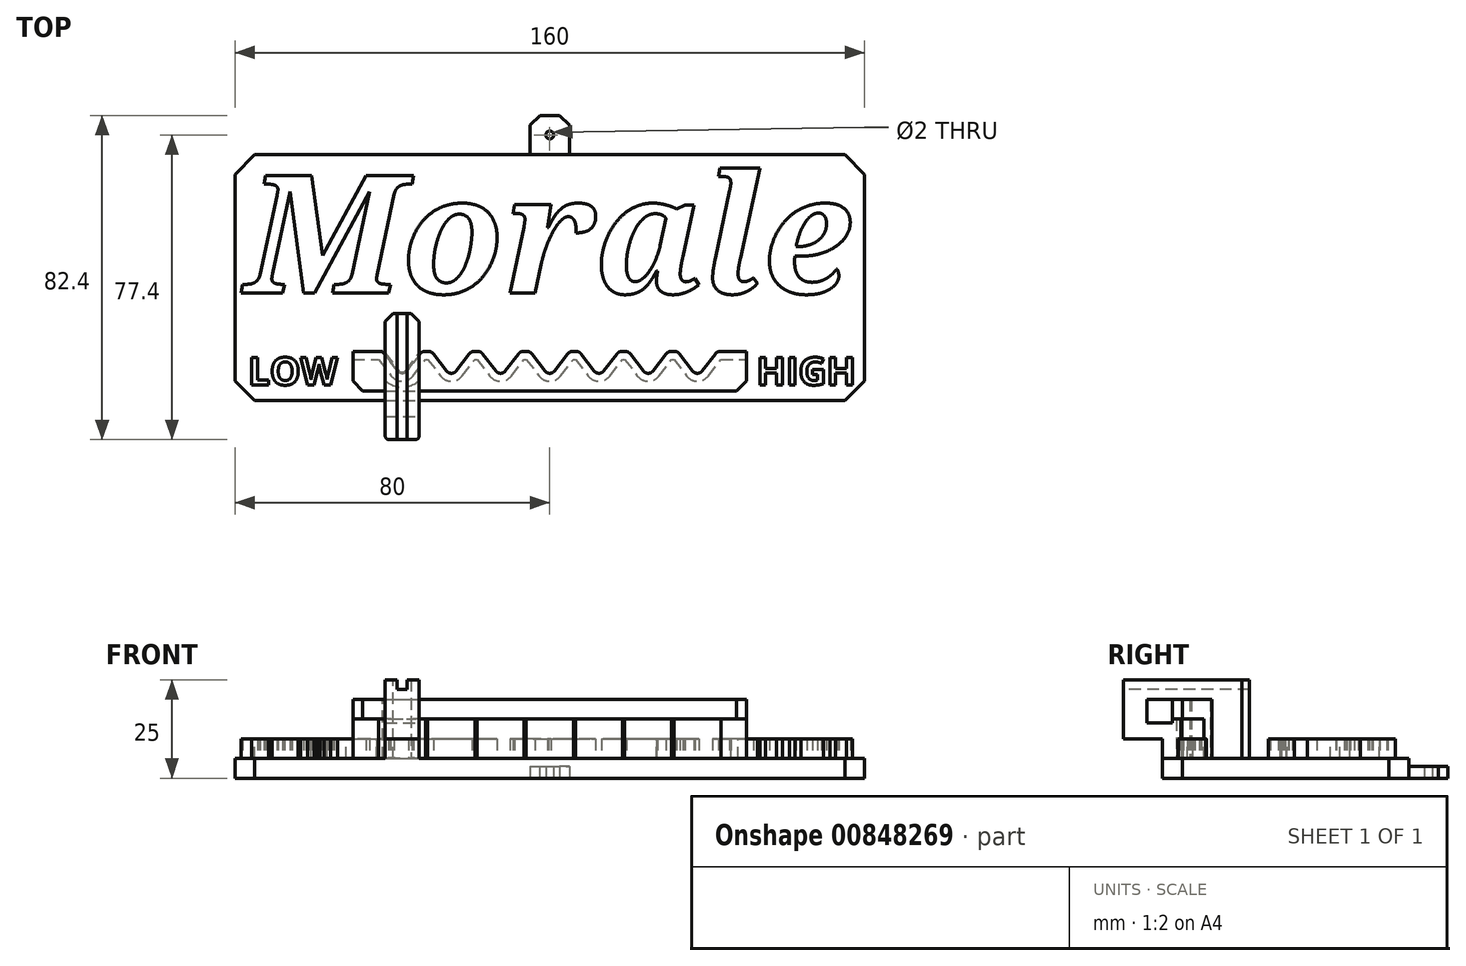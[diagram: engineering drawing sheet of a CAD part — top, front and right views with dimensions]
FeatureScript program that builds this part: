
annotation { "Feature Type Name" : "Feature", "Feature Type Description" : "" }
export const myFeature = defineFeature(function(context is Context, id is Id, definition is map)
    precondition{}
    {
        {
            var Q0;
            Q0=qCreatedBy(makeId("Top.planeOp"),FACE);
            var sketch = newSketch(context, id + "F0", { "sketchPlane" : qUnion([Q0])});
            skLineSegment(sketch, "E0.bottom", {"start": v(0, 0) * mm, "end": v(160, 0) * mm});
            skLineSegment(sketch, "E0.top", {"start": v(0, 37.5) * mm, "end": v(160, 37.5) * mm});
            skLineSegment(sketch, "E0.left", {"start": v(0, 0) * mm, "end": v(0, 37.5) * mm});
            skLineSegment(sketch, "E0.right", {"start": v(160, 0) * mm, "end": v(160, 37.5) * mm});
            skSolve(sketch);
        }
        {
            var Q0;
            Q0 = qSketchRegion(id + "F0", true);
            extrude(context, id + "F1", {"entities" : qUnion([Q0]), "depth" : 5 * mm, "offsetDistance" : 25 * mm});
        }
        {
            var Q0;
            Q0=makeQuery(id+"F1.opExtrude","CAP_FACE",FACE,{"disambiguationData":[OSD([sQuery(id+"F0.wireOp",EDGE,"E0.bottom"),sQuery(id+"F0.wireOp",EDGE,"E0.top"),sQuery(id+"F0.wireOp",EDGE,"E0.left"),sQuery(id+"F0.wireOp",EDGE,"E0.right")])],"isStart":false});
            var sketch = newSketch(context, id + "F2", { "sketchPlane" : qUnion([Q0])});
            skText(sketch, "E1", { "text": "Morale", "fontName": "NotoSerif-BoldItalic.ttf"});
            const initialGuessF2  = {"E1": [0.0025, 0.00232, 1, 0, 0.03018]};
            skSetInitialGuess(sketch, initialGuessF2);
            skSolve(sketch);
        }
        {
            var Q0;
            Q0 = qSketchRegion(id + "F2", true);
            extrude(context, id + "F3", {"entities" : qUnion([Q0]), "operationType" : NewBodyOperationType.ADD, "depth" : 5 * mm, "offsetDistance" : 25 * mm});
        }
        {
            var Q0;
            Q0=makeQuery(id+"F1.opExtrude","SWEPT_FACE",FACE,{"disambiguationData":[OSD([sQuery(id+"F0.wireOp",EDGE,"E0.bottom")])]});
            extrude(context, id + "F4", {"entities" : qUnion([Q0]), "operationType" : NewBodyOperationType.ADD, "depth" : 25 * mm, "offsetDistance" : 25 * mm});
        }
        {
            var Q0;
            {var subQ0=sQuery(id+"F0.wireOp",EDGE,"E0.bottom");var subQ1=sQuery(id+"F0.wireOp",EDGE,"E0.left");var subQ2=sQuery(id+"F0.wireOp",EDGE,"E0.right");var subQ3=sQuery(id+"F0.wireOp",EDGE,"E0.top");Q0=makeQuery(id+"F4.boolean.opBoolean","MERGE",FACE,{"derivedFrom":[makeQuery(id+"F3.boolean.opBoolean","SPLIT",FACE,{"disambiguationData":[TD([makeQuery(id+"F1.opExtrude","SWEPT_FACE",FACE,{"disambiguationData":[OSD([subQ0])]})])],"derivedFrom":makeQuery(id+"F1.opExtrude","CAP_FACE",FACE,{"disambiguationData":[OSD([subQ0,subQ3,subQ1,subQ2])],"isStart":false})}),makeQuery(id+"F4.opExtrude","SWEPT_FACE",FACE,{"disambiguationData":[OSD([subQ0]),TDD([makeQuery(id+"F1.opExtrude","CAP_EDGE",EDGE,{"disambiguationData":[OSD([subQ0])],"isStart":false})])]})]});}
            var sketch = newSketch(context, id + "F5", { "sketchPlane" : qUnion([Q0])});
            skLineSegment(sketch, "E2.bottom", {"start": v(30, -22.5) * mm, "end": v(130, -22.5) * mm});
            skLineSegment(sketch, "E2.top", {"start": v(30, -12.5) * mm, "end": v(130, -12.5) * mm});
            skLineSegment(sketch, "E2.left", {"start": v(30, -22.5) * mm, "end": v(30, -12.5) * mm});
            skLineSegment(sketch, "E2.right", {"start": v(130, -22.5) * mm, "end": v(130, -12.5) * mm});
            skPoint(sketch, "E2.middle", {"position": v(80, -17.5) * mm});
            skPoint(sketch, "E2.middle.positionSnap0", {"position": v(80, -25) * mm});
            skPoint(sketch, "E2.centerSnap0", {"position": v(80, -25) * mm});
            skSolve(sketch);
        }
        {
            var Q0;
            Q0 = qSketchRegion(id + "F5", true);
            extrude(context, id + "F6", {"entities" : qUnion([Q0]), "operationType" : NewBodyOperationType.ADD, "depth" : 15 * mm, "offsetDistance" : 25 * mm});
        }
        {
            var Q0;
            Q0=makeQuery(id+"F6.opExtrude","CAP_FACE",FACE,{"disambiguationData":[OSD([sQuery(id+"F5.wireOp",EDGE,"E2.bottom"),sQuery(id+"F5.wireOp",EDGE,"E2.top"),sQuery(id+"F5.wireOp",EDGE,"E2.left"),sQuery(id+"F5.wireOp",EDGE,"E2.right")])],"isStart":false});
            var sketch = newSketch(context, id + "F7", { "sketchPlane" : qUnion([Q0])});
            skLineSegment(sketch, "E3", {"start": v(37.5, -12.5) * mm, "end": v(42.5, -19.02) * mm});
            skLineSegment(sketch, "E4", {"start": v(42.5, -19.02) * mm, "end": v(47.5, -12.5) * mm});
            skLineSegment(sketch, "E5", {"start": v(37.5, -12.5) * mm, "end": v(47.5, -12.5) * mm});
            skLineSegment(sketch, "E6.1.0.0", {"start": v(50, -12.5) * mm, "end": v(60, -12.5) * mm});
            skLineSegment(sketch, "E6.1.0.1", {"start": v(55, -19.02) * mm, "end": v(60, -12.5) * mm});
            skLineSegment(sketch, "E6.1.0.2", {"start": v(50, -12.5) * mm, "end": v(55, -19.02) * mm});
            skLineSegment(sketch, "E6.2.0.0", {"start": v(62.5, -12.5) * mm, "end": v(72.5, -12.5) * mm});
            skLineSegment(sketch, "E6.2.0.1", {"start": v(67.5, -19.02) * mm, "end": v(72.5, -12.5) * mm});
            skLineSegment(sketch, "E6.2.0.2", {"start": v(62.5, -12.5) * mm, "end": v(67.5, -19.02) * mm});
            skLineSegment(sketch, "E6.3.0.0", {"start": v(75, -12.5) * mm, "end": v(85, -12.5) * mm});
            skLineSegment(sketch, "E6.3.0.1", {"start": v(80, -19.02) * mm, "end": v(85, -12.5) * mm});
            skLineSegment(sketch, "E6.3.0.2", {"start": v(75, -12.5) * mm, "end": v(80, -19.02) * mm});
            skLineSegment(sketch, "E6.4.0.0", {"start": v(87.5, -12.5) * mm, "end": v(97.5, -12.5) * mm});
            skLineSegment(sketch, "E6.4.0.1", {"start": v(92.5, -19.02) * mm, "end": v(97.5, -12.5) * mm});
            skLineSegment(sketch, "E6.4.0.2", {"start": v(87.5, -12.5) * mm, "end": v(92.5, -19.02) * mm});
            skLineSegment(sketch, "E6.5.0.0", {"start": v(100, -12.5) * mm, "end": v(110, -12.5) * mm});
            skLineSegment(sketch, "E6.5.0.1", {"start": v(105, -19.02) * mm, "end": v(110, -12.5) * mm});
            skLineSegment(sketch, "E6.5.0.2", {"start": v(100, -12.5) * mm, "end": v(105, -19.02) * mm});
            skLineSegment(sketch, "E6.6.0.0", {"start": v(112.5, -12.5) * mm, "end": v(122.5, -12.5) * mm});
            skLineSegment(sketch, "E6.6.0.1", {"start": v(117.5, -19.02) * mm, "end": v(122.5, -12.5) * mm});
            skLineSegment(sketch, "E6.6.0.2", {"start": v(112.5, -12.5) * mm, "end": v(117.5, -19.02) * mm});
            skLineSegment(sketch, "E6.direction1", {"start": v(42.5, -19.02) * mm, "end": v(55, -19.02) * mm, "construction": true});
            skSolve(sketch);
        }
        {
            var Q0;
            Q0 = qSketchRegion(id + "F7", true);
            var Q1;
            {var subQ0=sQuery(id+"F0.wireOp",EDGE,"E0.bottom");var subQ1=sQuery(id+"F0.wireOp",EDGE,"E0.left");var subQ2=sQuery(id+"F0.wireOp",EDGE,"E0.right");var subQ3=sQuery(id+"F0.wireOp",EDGE,"E0.top");Q1=makeQuery(id+"F4.boolean.opBoolean","MERGE",FACE,{"derivedFrom":[makeQuery(id+"F3.boolean.opBoolean","SPLIT",FACE,{"disambiguationData":[TD([makeQuery(id+"F1.opExtrude","SWEPT_FACE",FACE,{"disambiguationData":[OSD([subQ0])]})])],"derivedFrom":makeQuery(id+"F1.opExtrude","CAP_FACE",FACE,{"disambiguationData":[OSD([subQ0,subQ3,subQ1,subQ2])],"isStart":false})}),makeQuery(id+"F4.opExtrude","SWEPT_FACE",FACE,{"disambiguationData":[OSD([subQ0]),TDD([makeQuery(id+"F1.opExtrude","CAP_EDGE",EDGE,{"disambiguationData":[OSD([subQ0])],"isStart":false})])]})]});}
            extrude(context, id + "F8", {"entities" : qUnion([Q0]), "operationType" : NewBodyOperationType.REMOVE, "endBound" : BoundingType.UP_TO_SURFACE, "oppositeDirection" : true, "depth" : 25 * mm, "endBoundEntityFace" : qUnion([Q1]), "offsetDistance" : 25 * mm});
        }
        {
            var Q0;
            {var subQ0=sQuery(id+"F0.wireOp",EDGE,"E0.bottom");var subQ1=sQuery(id+"F0.wireOp",EDGE,"E0.left");var subQ2=sQuery(id+"F0.wireOp",EDGE,"E0.right");var subQ3=sQuery(id+"F0.wireOp",EDGE,"E0.top");Q0=makeQuery(id+"F8.boolean.opBoolean","MERGE",FACE,{"derivedFrom":[makeQuery(id+"F4.boolean.opBoolean","MERGE",FACE,{"derivedFrom":[makeQuery(id+"F3.boolean.opBoolean","SPLIT",FACE,{"disambiguationData":[TD([makeQuery(id+"F1.opExtrude","SWEPT_FACE",FACE,{"disambiguationData":[OSD([subQ0])]})])],"derivedFrom":makeQuery(id+"F1.opExtrude","CAP_FACE",FACE,{"disambiguationData":[OSD([subQ0,subQ3,subQ1,subQ2])],"isStart":false})}),makeQuery(id+"F4.opExtrude","SWEPT_FACE",FACE,{"disambiguationData":[OSD([subQ0]),TDD([makeQuery(id+"F1.opExtrude","CAP_EDGE",EDGE,{"disambiguationData":[OSD([subQ0])],"isStart":false})])]})]})],"fromTools":[makeQuery(id+"F8.opExtrude","CAP_FACE",FACE,{"disambiguationData":[OSD([sQuery(id+"F7.wireOp",EDGE,"E3"),sQuery(id+"F7.wireOp",EDGE,"E4"),sQuery(id+"F7.wireOp",EDGE,"E5")])],"isStart":false}),makeQuery(id+"F8.opExtrude","CAP_FACE",FACE,{"disambiguationData":[OSD([sQuery(id+"F7.wireOp",EDGE,"E6.1.0.0"),sQuery(id+"F7.wireOp",EDGE,"E6.1.0.1"),sQuery(id+"F7.wireOp",EDGE,"E6.1.0.2")])],"isStart":false}),makeQuery(id+"F8.opExtrude","CAP_FACE",FACE,{"disambiguationData":[OSD([sQuery(id+"F7.wireOp",EDGE,"E6.2.0.0"),sQuery(id+"F7.wireOp",EDGE,"E6.2.0.1"),sQuery(id+"F7.wireOp",EDGE,"E6.2.0.2")])],"isStart":false}),makeQuery(id+"F8.opExtrude","CAP_FACE",FACE,{"disambiguationData":[OSD([sQuery(id+"F7.wireOp",EDGE,"E6.3.0.0"),sQuery(id+"F7.wireOp",EDGE,"E6.3.0.1"),sQuery(id+"F7.wireOp",EDGE,"E6.3.0.2")])],"isStart":false}),makeQuery(id+"F8.opExtrude","CAP_FACE",FACE,{"disambiguationData":[OSD([sQuery(id+"F7.wireOp",EDGE,"E6.4.0.0"),sQuery(id+"F7.wireOp",EDGE,"E6.4.0.1"),sQuery(id+"F7.wireOp",EDGE,"E6.4.0.2")])],"isStart":false}),makeQuery(id+"F8.opExtrude","CAP_FACE",FACE,{"disambiguationData":[OSD([sQuery(id+"F7.wireOp",EDGE,"E6.5.0.0"),sQuery(id+"F7.wireOp",EDGE,"E6.5.0.1"),sQuery(id+"F7.wireOp",EDGE,"E6.5.0.2")])],"isStart":false}),makeQuery(id+"F8.opExtrude","CAP_FACE",FACE,{"disambiguationData":[OSD([sQuery(id+"F7.wireOp",EDGE,"E6.6.0.0"),sQuery(id+"F7.wireOp",EDGE,"E6.6.0.1"),sQuery(id+"F7.wireOp",EDGE,"E6.6.0.2")])],"isStart":false})]});}
            var sketch = newSketch(context, id + "F9", { "sketchPlane" : qUnion([Q0])});
            skText(sketch, "E7", { "text": "LOW", "fontName": "OpenSans-Bold.ttf"});
            skText(sketch, "E8", { "text": "HIGH", "fontName": "OpenSans-Bold.ttf"});
            const initialGuessF9  = {"E7": [0.00338, -0.021, 1, 0, 0.00703], "E8": [0.1325, -0.021, 1, 0, 0.00703]};
            skSetInitialGuess(sketch, initialGuessF9);
            skSolve(sketch);
        }
        {
            var Q0;
            Q0 = qSketchRegion(id + "F9", true);
            var Q1;
            Q1=makeQuery(id+"F3.opExtrude","CAP_FACE",FACE,{"disambiguationData":[OSD([sQuery(id+"F2.wireOp",EDGE,"E1.sketch_text.stroke-203"),sQuery(id+"F2.wireOp",EDGE,"E1.sketch_text.stroke-204"),sQuery(id+"F2.wireOp",EDGE,"E1.sketch_text.stroke-205"),sQuery(id+"F2.wireOp",EDGE,"E1.sketch_text.stroke-206"),sQuery(id+"F2.wireOp",EDGE,"E1.sketch_text.stroke-207"),sQuery(id+"F2.wireOp",EDGE,"E1.sketch_text.stroke-208"),sQuery(id+"F2.wireOp",EDGE,"E1.sketch_text.stroke-209"),sQuery(id+"F2.wireOp",EDGE,"E1.sketch_text.stroke-210"),sQuery(id+"F2.wireOp",EDGE,"E1.sketch_text.stroke-211"),sQuery(id+"F2.wireOp",EDGE,"E1.sketch_text.stroke-212"),sQuery(id+"F2.wireOp",EDGE,"E1.sketch_text.stroke-213"),sQuery(id+"F2.wireOp",EDGE,"E1.sketch_text.stroke-214"),sQuery(id+"F2.wireOp",EDGE,"E1.sketch_text.stroke-215"),sQuery(id+"F2.wireOp",EDGE,"E1.sketch_text.stroke-216"),sQuery(id+"F2.wireOp",EDGE,"E1.sketch_text.stroke-217"),sQuery(id+"F2.wireOp",EDGE,"E1.sketch_text.stroke-218"),sQuery(id+"F2.wireOp",EDGE,"E1.sketch_text.stroke-219"),sQuery(id+"F2.wireOp",EDGE,"E1.sketch_text.stroke-220"),sQuery(id+"F2.wireOp",EDGE,"E1.sketch_text.stroke-221"),sQuery(id+"F2.wireOp",EDGE,"E1.sketch_text.stroke-222"),sQuery(id+"F2.wireOp",EDGE,"E1.sketch_text.stroke-223"),sQuery(id+"F2.wireOp",EDGE,"E1.sketch_text.stroke-224"),sQuery(id+"F2.wireOp",EDGE,"E1.sketch_text.stroke-225"),sQuery(id+"F2.wireOp",EDGE,"E1.sketch_text.stroke-226"),sQuery(id+"F2.wireOp",EDGE,"E1.sketch_text.stroke-227"),sQuery(id+"F2.wireOp",EDGE,"E1.sketch_text.stroke-228"),sQuery(id+"F2.wireOp",EDGE,"E1.sketch_text.stroke-229"),sQuery(id+"F2.wireOp",EDGE,"E1.sketch_text.stroke-230"),sQuery(id+"F2.wireOp",EDGE,"E1.sketch_text.stroke-231"),sQuery(id+"F2.wireOp",EDGE,"E1.sketch_text.stroke-232"),sQuery(id+"F2.wireOp",EDGE,"E1.sketch_text.stroke-233"),sQuery(id+"F2.wireOp",EDGE,"E1.sketch_text.stroke-234"),sQuery(id+"F2.wireOp",EDGE,"E1.sketch_text.stroke-235"),sQuery(id+"F2.wireOp",EDGE,"E1.sketch_text.stroke-236"),sQuery(id+"F2.wireOp",EDGE,"E1.sketch_text.stroke-237"),sQuery(id+"F2.wireOp",EDGE,"E1.sketch_text.stroke-238"),sQuery(id+"F2.wireOp",EDGE,"E1.sketch_text.stroke-239"),sQuery(id+"F2.wireOp",EDGE,"E1.sketch_text.stroke-240"),sQuery(id+"F2.wireOp",EDGE,"E1.sketch_text.stroke-241"),sQuery(id+"F2.wireOp",EDGE,"E1.sketch_text.stroke-242"),sQuery(id+"F2.wireOp",EDGE,"E1.sketch_text.stroke-243"),sQuery(id+"F2.wireOp",EDGE,"E1.sketch_text.stroke-244"),sQuery(id+"F2.wireOp",EDGE,"E1.sketch_text.stroke-245")])],"isStart":false});
            extrude(context, id + "F10", {"entities" : qUnion([Q0]), "operationType" : NewBodyOperationType.ADD, "endBound" : BoundingType.UP_TO_SURFACE, "depth" : 25 * mm, "endBoundEntityFace" : qUnion([Q1]), "offsetDistance" : 25 * mm});
        }
        {
            var Q0;
            Q0=makeQuery(id+"F8.boolean.opBoolean","COPY",EDGE,{"derivedFrom":makeQuery(id+"F8.opExtrude","SWEPT_EDGE",EDGE,{"disambiguationData":[OSD([sQuery(id+"F7.wireOp",EDGE,"E6.5.0.1"),sQuery(id+"F7.wireOp",EDGE,"E6.5.0.2")])]})});
            var Q1;
            Q1=makeQuery(id+"F8.boolean.opBoolean","COPY",EDGE,{"derivedFrom":makeQuery(id+"F8.opExtrude","SWEPT_EDGE",EDGE,{"disambiguationData":[OSD([sQuery(id+"F7.wireOp",EDGE,"E6.6.0.1"),sQuery(id+"F7.wireOp",EDGE,"E6.6.0.2")])]})});
            var Q2;
            Q2=makeQuery(id+"F8.boolean.opBoolean","COPY",EDGE,{"derivedFrom":makeQuery(id+"F8.opExtrude","SWEPT_EDGE",EDGE,{"disambiguationData":[OSD([sQuery(id+"F7.wireOp",EDGE,"E6.4.0.1"),sQuery(id+"F7.wireOp",EDGE,"E6.4.0.2")])]})});
            var Q3;
            Q3=makeQuery(id+"F8.boolean.opBoolean","COPY",EDGE,{"derivedFrom":makeQuery(id+"F8.opExtrude","SWEPT_EDGE",EDGE,{"disambiguationData":[OSD([sQuery(id+"F7.wireOp",EDGE,"E6.3.0.1"),sQuery(id+"F7.wireOp",EDGE,"E6.3.0.2")])]})});
            var Q4;
            Q4=makeQuery(id+"F8.boolean.opBoolean","COPY",EDGE,{"derivedFrom":makeQuery(id+"F8.opExtrude","SWEPT_EDGE",EDGE,{"disambiguationData":[OSD([sQuery(id+"F7.wireOp",EDGE,"E6.2.0.1"),sQuery(id+"F7.wireOp",EDGE,"E6.2.0.2")])]})});
            var Q5;
            Q5=makeQuery(id+"F8.boolean.opBoolean","COPY",EDGE,{"derivedFrom":makeQuery(id+"F8.opExtrude","SWEPT_EDGE",EDGE,{"disambiguationData":[OSD([sQuery(id+"F7.wireOp",EDGE,"E6.1.0.1"),sQuery(id+"F7.wireOp",EDGE,"E6.1.0.2")])]})});
            var Q6;
            Q6=makeQuery(id+"F8.boolean.opBoolean","COPY",EDGE,{"derivedFrom":makeQuery(id+"F8.opExtrude","SWEPT_EDGE",EDGE,{"disambiguationData":[OSD([sQuery(id+"F7.wireOp",EDGE,"E3"),sQuery(id+"F7.wireOp",EDGE,"E4")])]})});
            var Q7;
            Q7=makeQuery(id+"F8.boolean.opBoolean","COPY",EDGE,{"derivedFrom":makeQuery(id+"F8.opExtrude","SWEPT_EDGE",EDGE,{"disambiguationData":[OSD([sQuery(id+"F5.wireOp",EDGE,"E2.top"),sQuery(id+"F7.wireOp",EDGE,"E6.6.0.0"),sQuery(id+"F7.wireOp",EDGE,"E6.6.0.1")])]})});
            var Q8;
            Q8=makeQuery(id+"F8.boolean.opBoolean","COPY",EDGE,{"derivedFrom":makeQuery(id+"F8.opExtrude","SWEPT_EDGE",EDGE,{"disambiguationData":[OSD([sQuery(id+"F5.wireOp",EDGE,"E2.top"),sQuery(id+"F7.wireOp",EDGE,"E6.6.0.0"),sQuery(id+"F7.wireOp",EDGE,"E6.6.0.2")])]})});
            var Q9;
            Q9=makeQuery(id+"F8.boolean.opBoolean","COPY",EDGE,{"derivedFrom":makeQuery(id+"F8.opExtrude","SWEPT_EDGE",EDGE,{"disambiguationData":[OSD([sQuery(id+"F5.wireOp",EDGE,"E2.top"),sQuery(id+"F7.wireOp",EDGE,"E6.5.0.0"),sQuery(id+"F7.wireOp",EDGE,"E6.5.0.1")])]})});
            var Q10;
            Q10=makeQuery(id+"F8.boolean.opBoolean","COPY",EDGE,{"derivedFrom":makeQuery(id+"F8.opExtrude","SWEPT_EDGE",EDGE,{"disambiguationData":[OSD([sQuery(id+"F5.wireOp",EDGE,"E2.top"),sQuery(id+"F7.wireOp",EDGE,"E6.5.0.0"),sQuery(id+"F7.wireOp",EDGE,"E6.5.0.2")])]})});
            var Q11;
            Q11=makeQuery(id+"F8.boolean.opBoolean","COPY",EDGE,{"derivedFrom":makeQuery(id+"F8.opExtrude","SWEPT_EDGE",EDGE,{"disambiguationData":[OSD([sQuery(id+"F5.wireOp",EDGE,"E2.top"),sQuery(id+"F7.wireOp",EDGE,"E6.4.0.0"),sQuery(id+"F7.wireOp",EDGE,"E6.4.0.1")])]})});
            var Q12;
            Q12=makeQuery(id+"F8.boolean.opBoolean","COPY",EDGE,{"derivedFrom":makeQuery(id+"F8.opExtrude","SWEPT_EDGE",EDGE,{"disambiguationData":[OSD([sQuery(id+"F5.wireOp",EDGE,"E2.top"),sQuery(id+"F7.wireOp",EDGE,"E6.4.0.0"),sQuery(id+"F7.wireOp",EDGE,"E6.4.0.2")])]})});
            var Q13;
            Q13=makeQuery(id+"F8.boolean.opBoolean","COPY",EDGE,{"derivedFrom":makeQuery(id+"F8.opExtrude","SWEPT_EDGE",EDGE,{"disambiguationData":[OSD([sQuery(id+"F5.wireOp",EDGE,"E2.top"),sQuery(id+"F7.wireOp",EDGE,"E6.3.0.0"),sQuery(id+"F7.wireOp",EDGE,"E6.3.0.1")])]})});
            var Q14;
            Q14=makeQuery(id+"F8.boolean.opBoolean","COPY",EDGE,{"derivedFrom":makeQuery(id+"F8.opExtrude","SWEPT_EDGE",EDGE,{"disambiguationData":[OSD([sQuery(id+"F5.wireOp",EDGE,"E2.top"),sQuery(id+"F7.wireOp",EDGE,"E6.2.0.0"),sQuery(id+"F7.wireOp",EDGE,"E6.2.0.1")])]})});
            var Q15;
            Q15=makeQuery(id+"F8.boolean.opBoolean","COPY",EDGE,{"derivedFrom":makeQuery(id+"F8.opExtrude","SWEPT_EDGE",EDGE,{"disambiguationData":[OSD([sQuery(id+"F5.wireOp",EDGE,"E2.top"),sQuery(id+"F7.wireOp",EDGE,"E6.3.0.0"),sQuery(id+"F7.wireOp",EDGE,"E6.3.0.2")])]})});
            var Q16;
            Q16=makeQuery(id+"F8.boolean.opBoolean","COPY",EDGE,{"derivedFrom":makeQuery(id+"F8.opExtrude","SWEPT_EDGE",EDGE,{"disambiguationData":[OSD([sQuery(id+"F5.wireOp",EDGE,"E2.top"),sQuery(id+"F7.wireOp",EDGE,"E6.1.0.0"),sQuery(id+"F7.wireOp",EDGE,"E6.1.0.1")])]})});
            var Q17;
            Q17=makeQuery(id+"F8.boolean.opBoolean","COPY",EDGE,{"derivedFrom":makeQuery(id+"F8.opExtrude","SWEPT_EDGE",EDGE,{"disambiguationData":[OSD([sQuery(id+"F5.wireOp",EDGE,"E2.top"),sQuery(id+"F7.wireOp",EDGE,"E6.1.0.0"),sQuery(id+"F7.wireOp",EDGE,"E6.1.0.2")])]})});
            var Q18;
            Q18=makeQuery(id+"F8.boolean.opBoolean","COPY",EDGE,{"derivedFrom":makeQuery(id+"F8.opExtrude","SWEPT_EDGE",EDGE,{"disambiguationData":[OSD([sQuery(id+"F5.wireOp",EDGE,"E2.top"),sQuery(id+"F7.wireOp",EDGE,"E6.2.0.0"),sQuery(id+"F7.wireOp",EDGE,"E6.2.0.2")])]})});
            var Q19;
            Q19=makeQuery(id+"F8.boolean.opBoolean","COPY",EDGE,{"derivedFrom":makeQuery(id+"F8.opExtrude","SWEPT_EDGE",EDGE,{"disambiguationData":[OSD([sQuery(id+"F5.wireOp",EDGE,"E2.top"),sQuery(id+"F7.wireOp",EDGE,"E4"),sQuery(id+"F7.wireOp",EDGE,"E5")])]})});
            var Q20;
            Q20=makeQuery(id+"F8.boolean.opBoolean","COPY",EDGE,{"derivedFrom":makeQuery(id+"F8.opExtrude","SWEPT_EDGE",EDGE,{"disambiguationData":[OSD([sQuery(id+"F5.wireOp",EDGE,"E2.top"),sQuery(id+"F7.wireOp",EDGE,"E3"),sQuery(id+"F7.wireOp",EDGE,"E5")])]})});
            fillet(context, id + "F11", {"entities" : qUnion([Q0, Q1, Q2, Q3, Q4, Q5, Q6, Q7, Q8, Q9, Q10, Q11, Q12, Q13, Q14, Q15, Q16, Q17, Q18, Q19, Q20]), "radius" : 1.5 * mm, "tangentPropagation" : true, "allowEdgeOverflow" : false});
        }
        {
            var Q0;
            Q0=makeQuery(id+"F6.opExtrude","CAP_FACE",FACE,{"disambiguationData":[OSD([sQuery(id+"F5.wireOp",EDGE,"E2.bottom"),sQuery(id+"F5.wireOp",EDGE,"E2.top"),sQuery(id+"F5.wireOp",EDGE,"E2.left"),sQuery(id+"F5.wireOp",EDGE,"E2.right")])],"isStart":false});
            cPlane(context, id + "F12", {"entities" : qUnion([Q0]), "cplaneType" : CPlaneType.OFFSET, "offset" : 5 * mm, "oppositeDirection" : true, "width" : 150 * mm, "height" : 150 * mm});
        }
        {
            var Q0;
            Q0=qCreatedBy(id+"F12.planeOp",FACE);
            var sketch = newSketch(context, id + "F13", { "sketchPlane" : qUnion([Q0])});
            skArc(sketch, "E9.0", {"start": v(120.28, -18.68) * mm, "mid": v(117.5, -20.05) * mm, "end": v(114.72, -18.68) * mm});
            skLineSegment(sketch, "E9.1", {"start": v(123.49, -14.5) * mm, "end": v(120.28, -18.68) * mm});
            skLineSegment(sketch, "E9.2", {"start": v(130, -14.5) * mm, "end": v(123.49, -14.5) * mm});
            skLineSegment(sketch, "E9.6", {"start": v(36.51, -14.5) * mm, "end": v(30, -14.5) * mm});
            skLineSegment(sketch, "E9.7", {"start": v(39.72, -18.68) * mm, "end": v(36.51, -14.5) * mm});
            skArc(sketch, "E9.8", {"start": v(45.28, -18.68) * mm, "mid": v(42.5, -20.05) * mm, "end": v(39.72, -18.68) * mm});
            skLineSegment(sketch, "E9.9", {"start": v(85.99, -14.5) * mm, "end": v(82.78, -18.68) * mm});
            skLineSegment(sketch, "E9.10", {"start": v(86.51, -14.5) * mm, "end": v(85.99, -14.5) * mm});
            skLineSegment(sketch, "E9.11", {"start": v(89.72, -18.68) * mm, "end": v(86.51, -14.5) * mm});
            skArc(sketch, "E9.12", {"start": v(95.28, -18.68) * mm, "mid": v(92.5, -20.05) * mm, "end": v(89.72, -18.68) * mm});
            skLineSegment(sketch, "E9.13", {"start": v(98.49, -14.5) * mm, "end": v(95.28, -18.68) * mm});
            skLineSegment(sketch, "E9.14", {"start": v(99.01, -14.5) * mm, "end": v(98.49, -14.5) * mm});
            skLineSegment(sketch, "E9.15", {"start": v(111.51, -14.5) * mm, "end": v(110.99, -14.5) * mm});
            skLineSegment(sketch, "E9.16", {"start": v(110.99, -14.5) * mm, "end": v(107.78, -18.68) * mm});
            skArc(sketch, "E9.17", {"start": v(107.78, -18.68) * mm, "mid": v(105, -20.05) * mm, "end": v(102.22, -18.68) * mm});
            skLineSegment(sketch, "E9.18", {"start": v(102.22, -18.68) * mm, "end": v(99.01, -14.5) * mm});
            skArc(sketch, "E9.19", {"start": v(82.78, -18.68) * mm, "mid": v(80, -20.05) * mm, "end": v(77.22, -18.68) * mm});
            skLineSegment(sketch, "E9.20", {"start": v(77.22, -18.68) * mm, "end": v(74.01, -14.5) * mm});
            skLineSegment(sketch, "E9.21", {"start": v(74.01, -14.5) * mm, "end": v(73.49, -14.5) * mm});
            skLineSegment(sketch, "E9.22", {"start": v(73.49, -14.5) * mm, "end": v(70.28, -18.68) * mm});
            skArc(sketch, "E9.23", {"start": v(70.28, -18.68) * mm, "mid": v(67.5, -20.05) * mm, "end": v(64.72, -18.68) * mm});
            skLineSegment(sketch, "E9.24", {"start": v(64.72, -18.68) * mm, "end": v(61.51, -14.5) * mm});
            skLineSegment(sketch, "E9.25", {"start": v(61.51, -14.5) * mm, "end": v(60.99, -14.5) * mm});
            skLineSegment(sketch, "E9.26", {"start": v(60.99, -14.5) * mm, "end": v(57.78, -18.68) * mm});
            skArc(sketch, "E9.27", {"start": v(57.78, -18.68) * mm, "mid": v(55, -20.05) * mm, "end": v(52.22, -18.68) * mm});
            skLineSegment(sketch, "E9.28", {"start": v(114.72, -18.68) * mm, "end": v(111.51, -14.5) * mm});
            skLineSegment(sketch, "E9.29", {"start": v(52.22, -18.68) * mm, "end": v(49.01, -14.5) * mm});
            skLineSegment(sketch, "E9.30", {"start": v(49.01, -14.5) * mm, "end": v(48.49, -14.5) * mm});
            skLineSegment(sketch, "E9.31", {"start": v(48.49, -14.5) * mm, "end": v(45.28, -18.68) * mm});
            skLineSegment(sketch, "E10.0", {"start": v(30, -22.5) * mm, "end": v(130, -22.5) * mm});
            skLineSegment(sketch, "E11.0", {"start": v(30, -22.5) * mm, "end": v(30, -14.5) * mm});
            skLineSegment(sketch, "E12.0", {"start": v(130, -22.5) * mm, "end": v(130, -14.5) * mm});
            skPoint(sketch, "E13.orphan", {"position": v(30, -12.5) * mm});
            skPoint(sketch, "E14.orphan", {"position": v(130, -12.5) * mm});
            skSolve(sketch);
        }
        {
            var Q0;
            Q0 = qSketchRegion(id + "F13", true);
            var Q1;
            {var subQ117=sQuery(id+"F0.wireOp",EDGE,"E0.top");var subQ118=makeQuery(id+"F1.opExtrude","SWEPT_FACE",FACE,{"disambiguationData":[OSD([subQ117])]});var subQ124=sQuery(id+"F0.wireOp",EDGE,"E0.left");var subQ134=sQuery(id+"F0.wireOp",EDGE,"E0.right");var subQ208=sQuery(id+"F0.wireOp",EDGE,"E0.bottom");var subQ209=sQuery(id+"F7.wireOp",EDGE,"E3");var subQ210=sQuery(id+"F7.wireOp",EDGE,"E4");var subQ211=sQuery(id+"F7.wireOp",EDGE,"E6.1.0.1");var subQ212=sQuery(id+"F7.wireOp",EDGE,"E6.1.0.2");var subQ213=sQuery(id+"F7.wireOp",EDGE,"E6.2.0.1");var subQ214=sQuery(id+"F7.wireOp",EDGE,"E6.2.0.2");var subQ215=sQuery(id+"F7.wireOp",EDGE,"E6.3.0.1");var subQ216=sQuery(id+"F7.wireOp",EDGE,"E6.3.0.2");var subQ217=sQuery(id+"F7.wireOp",EDGE,"E6.4.0.1");var subQ218=sQuery(id+"F7.wireOp",EDGE,"E6.4.0.2");var subQ219=sQuery(id+"F7.wireOp",EDGE,"E6.5.0.1");var subQ220=sQuery(id+"F7.wireOp",EDGE,"E6.5.0.2");var subQ221=sQuery(id+"F7.wireOp",EDGE,"E6.6.0.1");var subQ222=sQuery(id+"F7.wireOp",EDGE,"E6.6.0.2");Q1=makeQuery(id+"F10.boolean.opBoolean","SPLIT",FACE,{"disambiguationData":[TD([subQ118])],"derivedFrom":makeQuery(id+"F8.boolean.opBoolean","MERGE",FACE,{"derivedFrom":[makeQuery(id+"F4.boolean.opBoolean","MERGE",FACE,{"derivedFrom":[makeQuery(id+"F3.boolean.opBoolean","SPLIT",FACE,{"disambiguationData":[TD([makeQuery(id+"F1.opExtrude","SWEPT_FACE",FACE,{"disambiguationData":[OSD([subQ208])]})])],"derivedFrom":makeQuery(id+"F1.opExtrude","CAP_FACE",FACE,{"disambiguationData":[OSD([subQ208,subQ117,subQ124,subQ134])],"isStart":false})}),makeQuery(id+"F4.opExtrude","SWEPT_FACE",FACE,{"disambiguationData":[OSD([subQ208]),TDD([makeQuery(id+"F1.opExtrude","CAP_EDGE",EDGE,{"disambiguationData":[OSD([subQ208])],"isStart":false})])]})]})],"fromTools":[makeQuery(id+"F8.opExtrude","CAP_FACE",FACE,{"disambiguationData":[OSD([subQ209,subQ210,sQuery(id+"F7.wireOp",EDGE,"E5")])],"isStart":false}),makeQuery(id+"F8.opExtrude","CAP_FACE",FACE,{"disambiguationData":[OSD([sQuery(id+"F7.wireOp",EDGE,"E6.1.0.0"),subQ211,subQ212])],"isStart":false}),makeQuery(id+"F8.opExtrude","CAP_FACE",FACE,{"disambiguationData":[OSD([sQuery(id+"F7.wireOp",EDGE,"E6.2.0.0"),subQ213,subQ214])],"isStart":false}),makeQuery(id+"F8.opExtrude","CAP_FACE",FACE,{"disambiguationData":[OSD([sQuery(id+"F7.wireOp",EDGE,"E6.3.0.0"),subQ215,subQ216])],"isStart":false}),makeQuery(id+"F8.opExtrude","CAP_FACE",FACE,{"disambiguationData":[OSD([sQuery(id+"F7.wireOp",EDGE,"E6.4.0.0"),subQ217,subQ218])],"isStart":false}),makeQuery(id+"F8.opExtrude","CAP_FACE",FACE,{"disambiguationData":[OSD([sQuery(id+"F7.wireOp",EDGE,"E6.5.0.0"),subQ219,subQ220])],"isStart":false}),makeQuery(id+"F8.opExtrude","CAP_FACE",FACE,{"disambiguationData":[OSD([sQuery(id+"F7.wireOp",EDGE,"E6.6.0.0"),subQ221,subQ222])],"isStart":false})]})});}
            extrude(context, id + "F14", {"entities" : qUnion([Q0]), "operationType" : NewBodyOperationType.REMOVE, "endBound" : BoundingType.UP_TO_SURFACE, "oppositeDirection" : true, "depth" : 25 * mm, "endBoundEntityFace" : qUnion([Q1]), "offsetDistance" : 25 * mm});
        }
        {
            var Q0;
            Q0=makeQuery(id+"F1.opExtrude","SWEPT_EDGE",EDGE,{"disambiguationData":[OSD([sQuery(id+"F0.wireOp",EDGE,"E0.top"),sQuery(id+"F0.wireOp",EDGE,"E0.left")])]});
            var Q1;
            Q1=makeQuery(id+"F4.opExtrude","CAP_EDGE",EDGE,{"disambiguationData":[OSD([sQuery(id+"F0.wireOp",EDGE,"E0.bottom"),sQuery(id+"F0.wireOp",EDGE,"E0.left")])],"isStart":false});
            var Q2;
            Q2=makeQuery(id+"F1.opExtrude","SWEPT_EDGE",EDGE,{"disambiguationData":[OSD([sQuery(id+"F0.wireOp",EDGE,"E0.top"),sQuery(id+"F0.wireOp",EDGE,"E0.right")])]});
            var Q3;
            Q3=makeQuery(id+"F4.opExtrude","CAP_EDGE",EDGE,{"disambiguationData":[OSD([sQuery(id+"F0.wireOp",EDGE,"E0.bottom"),sQuery(id+"F0.wireOp",EDGE,"E0.right")])],"isStart":false});
            chamfer(context, id + "F15", {"entities" : qUnion([Q0, Q1, Q2, Q3]), "width" : 5 * mm, "tangentPropagation" : true});
        }
        {
            var Q0;
            Q0=makeQuery(id+"F6.opExtrude","SWEPT_EDGE",EDGE,{"disambiguationData":[OSD([sQuery(id+"F5.wireOp",EDGE,"E2.bottom"),sQuery(id+"F5.wireOp",EDGE,"E2.left")])]});
            var Q1;
            Q1=makeQuery(id+"F6.opExtrude","SWEPT_EDGE",EDGE,{"disambiguationData":[OSD([sQuery(id+"F5.wireOp",EDGE,"E2.bottom"),sQuery(id+"F5.wireOp",EDGE,"E2.right")])]});
            chamfer(context, id + "F16", {"entities" : qUnion([Q0, Q1]), "width" : 2.5 * mm, "tangentPropagation" : true});
        }
        {
            var Q0;
            {var subQ117=sQuery(id+"F0.wireOp",EDGE,"E0.top");var subQ118=makeQuery(id+"F1.opExtrude","SWEPT_FACE",FACE,{"disambiguationData":[OSD([subQ117])]});var subQ124=sQuery(id+"F0.wireOp",EDGE,"E0.left");var subQ134=sQuery(id+"F0.wireOp",EDGE,"E0.right");var subQ208=sQuery(id+"F0.wireOp",EDGE,"E0.bottom");var subQ209=sQuery(id+"F7.wireOp",EDGE,"E3");var subQ210=sQuery(id+"F7.wireOp",EDGE,"E4");var subQ211=sQuery(id+"F7.wireOp",EDGE,"E6.1.0.1");var subQ212=sQuery(id+"F7.wireOp",EDGE,"E6.1.0.2");var subQ213=sQuery(id+"F7.wireOp",EDGE,"E6.2.0.1");var subQ214=sQuery(id+"F7.wireOp",EDGE,"E6.2.0.2");var subQ215=sQuery(id+"F7.wireOp",EDGE,"E6.3.0.1");var subQ216=sQuery(id+"F7.wireOp",EDGE,"E6.3.0.2");var subQ217=sQuery(id+"F7.wireOp",EDGE,"E6.4.0.1");var subQ218=sQuery(id+"F7.wireOp",EDGE,"E6.4.0.2");var subQ219=sQuery(id+"F7.wireOp",EDGE,"E6.5.0.1");var subQ220=sQuery(id+"F7.wireOp",EDGE,"E6.5.0.2");var subQ221=sQuery(id+"F7.wireOp",EDGE,"E6.6.0.1");var subQ222=sQuery(id+"F7.wireOp",EDGE,"E6.6.0.2");Q0=makeQuery(id+"F14.boolean.opBoolean","MERGE",FACE,{"derivedFrom":[makeQuery(id+"F10.boolean.opBoolean","SPLIT",FACE,{"disambiguationData":[TD([subQ118])],"derivedFrom":makeQuery(id+"F8.boolean.opBoolean","MERGE",FACE,{"derivedFrom":[makeQuery(id+"F4.boolean.opBoolean","MERGE",FACE,{"derivedFrom":[makeQuery(id+"F3.boolean.opBoolean","SPLIT",FACE,{"disambiguationData":[TD([makeQuery(id+"F1.opExtrude","SWEPT_FACE",FACE,{"disambiguationData":[OSD([subQ208])]})])],"derivedFrom":makeQuery(id+"F1.opExtrude","CAP_FACE",FACE,{"disambiguationData":[OSD([subQ208,subQ117,subQ124,subQ134])],"isStart":false})}),makeQuery(id+"F4.opExtrude","SWEPT_FACE",FACE,{"disambiguationData":[OSD([subQ208]),TDD([makeQuery(id+"F1.opExtrude","CAP_EDGE",EDGE,{"disambiguationData":[OSD([subQ208])],"isStart":false})])]})]})],"fromTools":[makeQuery(id+"F8.opExtrude","CAP_FACE",FACE,{"disambiguationData":[OSD([subQ209,subQ210,sQuery(id+"F7.wireOp",EDGE,"E5")])],"isStart":false}),makeQuery(id+"F8.opExtrude","CAP_FACE",FACE,{"disambiguationData":[OSD([sQuery(id+"F7.wireOp",EDGE,"E6.1.0.0"),subQ211,subQ212])],"isStart":false}),makeQuery(id+"F8.opExtrude","CAP_FACE",FACE,{"disambiguationData":[OSD([sQuery(id+"F7.wireOp",EDGE,"E6.2.0.0"),subQ213,subQ214])],"isStart":false}),makeQuery(id+"F8.opExtrude","CAP_FACE",FACE,{"disambiguationData":[OSD([sQuery(id+"F7.wireOp",EDGE,"E6.3.0.0"),subQ215,subQ216])],"isStart":false}),makeQuery(id+"F8.opExtrude","CAP_FACE",FACE,{"disambiguationData":[OSD([sQuery(id+"F7.wireOp",EDGE,"E6.4.0.0"),subQ217,subQ218])],"isStart":false}),makeQuery(id+"F8.opExtrude","CAP_FACE",FACE,{"disambiguationData":[OSD([sQuery(id+"F7.wireOp",EDGE,"E6.5.0.0"),subQ219,subQ220])],"isStart":false}),makeQuery(id+"F8.opExtrude","CAP_FACE",FACE,{"disambiguationData":[OSD([sQuery(id+"F7.wireOp",EDGE,"E6.6.0.0"),subQ221,subQ222])],"isStart":false})]})})],"fromTools":[makeQuery(id+"F14.opExtrude","CAP_FACE",FACE,{"disambiguationData":[OSD([sQuery(id+"F13.wireOp",EDGE,"E9.0"),sQuery(id+"F13.wireOp",EDGE,"E9.1"),sQuery(id+"F13.wireOp",EDGE,"E9.2"),sQuery(id+"F13.wireOp",EDGE,"E9.6"),sQuery(id+"F13.wireOp",EDGE,"E9.7"),sQuery(id+"F13.wireOp",EDGE,"E9.8"),sQuery(id+"F13.wireOp",EDGE,"E9.9"),sQuery(id+"F13.wireOp",EDGE,"E9.10"),sQuery(id+"F13.wireOp",EDGE,"E9.11"),sQuery(id+"F13.wireOp",EDGE,"E9.12"),sQuery(id+"F13.wireOp",EDGE,"E9.13"),sQuery(id+"F13.wireOp",EDGE,"E9.14"),sQuery(id+"F13.wireOp",EDGE,"E9.15"),sQuery(id+"F13.wireOp",EDGE,"E9.16"),sQuery(id+"F13.wireOp",EDGE,"E9.17"),sQuery(id+"F13.wireOp",EDGE,"E9.18"),sQuery(id+"F13.wireOp",EDGE,"E9.19"),sQuery(id+"F13.wireOp",EDGE,"E9.20"),sQuery(id+"F13.wireOp",EDGE,"E9.21"),sQuery(id+"F13.wireOp",EDGE,"E9.22"),sQuery(id+"F13.wireOp",EDGE,"E9.23"),sQuery(id+"F13.wireOp",EDGE,"E9.24"),sQuery(id+"F13.wireOp",EDGE,"E9.25"),sQuery(id+"F13.wireOp",EDGE,"E9.26"),sQuery(id+"F13.wireOp",EDGE,"E9.27"),sQuery(id+"F13.wireOp",EDGE,"E9.28"),sQuery(id+"F13.wireOp",EDGE,"E9.29"),sQuery(id+"F13.wireOp",EDGE,"E9.30"),sQuery(id+"F13.wireOp",EDGE,"E9.31"),sQuery(id+"F13.wireOp",EDGE,"E10.0"),sQuery(id+"F13.wireOp",EDGE,"E11.0"),sQuery(id+"F13.wireOp",EDGE,"E12.0")])],"isStart":false})]});}
            var sketch = newSketch(context, id + "F17", { "sketchPlane" : qUnion([Q0])});
            skLineSegment(sketch, "E15.0", {"start": v(43.45, -17.28) * mm, "end": v(46.81, -12.9) * mm});
            skArc(sketch, "E15.1", {"start": v(43.45, -17.28) * mm, "mid": v(42.5, -17.75) * mm, "end": v(41.55, -17.28) * mm});
            skLineSegment(sketch, "E15.2", {"start": v(38.19, -12.9) * mm, "end": v(41.55, -17.28) * mm});
            skArc(sketch, "E16.1", {"start": v(38.19, -19.9) * mm, "mid": v(42.5, -21.54) * mm, "end": v(46.81, -19.9) * mm});
            skLineSegment(sketch, "E17", {"start": v(38.19, -12.9) * mm, "end": v(38.19, -2.9) * mm});
            skLineSegment(sketch, "E18", {"start": v(38.19, -2.9) * mm, "end": v(46.81, -2.9) * mm});
            skLineSegment(sketch, "E19", {"start": v(46.81, -2.9) * mm, "end": v(46.81, -12.9) * mm});
            skLineSegment(sketch, "E20", {"start": v(38.19, -12.9) * mm, "end": v(38.19, -19.9) * mm, "construction": true});
            skLineSegment(sketch, "E21", {"start": v(38.19, -19.9) * mm, "end": v(46.81, -19.9) * mm, "construction": true});
            skLineSegment(sketch, "E22", {"start": v(46.81, -19.9) * mm, "end": v(46.81, -12.9) * mm, "construction": true});
            skLineSegment(sketch, "E23", {"start": v(38.19, -19.9) * mm, "end": v(38.19, -34.9) * mm});
            skLineSegment(sketch, "E24", {"start": v(38.19, -34.9) * mm, "end": v(46.81, -34.9) * mm});
            skLineSegment(sketch, "E25", {"start": v(46.81, -34.9) * mm, "end": v(46.81, -19.9) * mm});
            skSolve(sketch);
        }
        {
            var Q0;
            Q0 = qSketchRegion(id + "F17", true);
            extrude(context, id + "F18", {"entities" : qUnion([Q0]), "depth" : 10 * mm, "offsetDistance" : 25 * mm});
        }
        {
            var Q0;
            Q0=makeQuery(id+"F18.opExtrude","CAP_FACE",FACE,{"disambiguationData":[OSD([sQuery(id+"F17.wireOp",EDGE,"E16.1"),sQuery(id+"F17.wireOp",EDGE,"E23"),sQuery(id+"F17.wireOp",EDGE,"E24"),sQuery(id+"F17.wireOp",EDGE,"E25")])],"isStart":false});
            var sketch = newSketch(context, id + "F19", { "sketchPlane" : qUnion([Q0])});
            skLineSegment(sketch, "E26.bottom", {"start": v(38.19, -34.9) * mm, "end": v(46.81, -34.9) * mm});
            skLineSegment(sketch, "E26.top", {"start": v(38.19, -29) * mm, "end": v(46.81, -29) * mm});
            skLineSegment(sketch, "E26.left", {"start": v(38.19, -34.9) * mm, "end": v(38.19, -29) * mm});
            skLineSegment(sketch, "E26.right", {"start": v(46.81, -34.9) * mm, "end": v(46.81, -29) * mm});
            skLineSegment(sketch, "E27.0.0", {"start": v(46.81, -12.9) * mm, "end": v(46.81, -2.9) * mm});
            skLineSegment(sketch, "E27.0.1", {"start": v(46.81, -2.9) * mm, "end": v(38.19, -2.9) * mm});
            skLineSegment(sketch, "E27.0.2", {"start": v(38.19, -2.9) * mm, "end": v(38.19, -12.9) * mm});
            skLineSegment(sketch, "E27.0.3", {"start": v(38.19, -12.9) * mm, "end": v(41.55, -17.28) * mm});
            skArc(sketch, "E27.0.4", {"start": v(41.55, -17.28) * mm, "mid": v(42.5, -17.75) * mm, "end": v(43.45, -17.28) * mm});
            skLineSegment(sketch, "E27.0.5", {"start": v(43.45, -17.28) * mm, "end": v(46.81, -12.9) * mm});
            skSolve(sketch);
        }
        {
            var Q0;
            Q0 = qSketchRegion(id + "F19", true);
            var Q1;
            Q1=makeQuery(id+"F6.opExtrude","CAP_FACE",FACE,{"disambiguationData":[OSD([sQuery(id+"F5.wireOp",EDGE,"E2.bottom"),sQuery(id+"F5.wireOp",EDGE,"E2.top"),sQuery(id+"F5.wireOp",EDGE,"E2.left"),sQuery(id+"F5.wireOp",EDGE,"E2.right")])],"isStart":false});
            extrude(context, id + "F20", {"entities" : qUnion([Q0]), "operationType" : NewBodyOperationType.ADD, "endBound" : BoundingType.UP_TO_SURFACE, "depth" : 25 * mm, "endBoundEntityFace" : qUnion([Q1]), "offsetDistance" : 25 * mm});
        }
        {
            var Q0;
            Q0=makeQuery(id+"F20.opExtrude","CAP_FACE",FACE,{"disambiguationData":[OSD([sQuery(id+"F19.wireOp",EDGE,"E27.0.0"),sQuery(id+"F19.wireOp",EDGE,"E27.0.1"),sQuery(id+"F19.wireOp",EDGE,"E27.0.2"),sQuery(id+"F19.wireOp",EDGE,"E27.0.3"),sQuery(id+"F19.wireOp",EDGE,"E27.0.4"),sQuery(id+"F19.wireOp",EDGE,"E27.0.5")])],"isStart":false});
            var sketch = newSketch(context, id + "F21", { "sketchPlane" : qUnion([Q0])});
            skLineSegment(sketch, "E28.0.0", {"start": v(38.19, -12.9) * mm, "end": v(41.55, -17.28) * mm, "construction": true});
            skArc(sketch, "E28.0.1", {"start": v(41.55, -17.28) * mm, "mid": v(42.5, -17.75) * mm, "end": v(43.45, -17.28) * mm, "construction": true});
            skLineSegment(sketch, "E28.0.2", {"start": v(43.45, -17.28) * mm, "end": v(46.81, -12.9) * mm, "construction": true});
            skLineSegment(sketch, "E28.0.3", {"start": v(46.81, -12.9) * mm, "end": v(46.81, -2.9) * mm, "construction": true});
            skLineSegment(sketch, "E28.0.4", {"start": v(46.81, -2.9) * mm, "end": v(38.19, -2.9) * mm, "construction": true});
            skLineSegment(sketch, "E28.0.5", {"start": v(38.19, -2.9) * mm, "end": v(38.19, -12.9) * mm, "construction": true});
            skLineSegment(sketch, "E29.0.0", {"start": v(46.81, -29) * mm, "end": v(38.19, -29) * mm, "construction": true});
            skLineSegment(sketch, "E29.0.1", {"start": v(38.19, -29) * mm, "end": v(38.19, -34.9) * mm, "construction": true});
            skLineSegment(sketch, "E29.0.2", {"start": v(38.19, -34.9) * mm, "end": v(46.81, -34.9) * mm, "construction": true});
            skLineSegment(sketch, "E29.0.3", {"start": v(46.81, -34.9) * mm, "end": v(46.81, -29) * mm, "construction": true});
            skLineSegment(sketch, "E30.bottom", {"start": v(38.19, -34.9) * mm, "end": v(46.81, -34.9) * mm});
            skLineSegment(sketch, "E30.top", {"start": v(38.19, -2.9) * mm, "end": v(46.81, -2.9) * mm});
            skLineSegment(sketch, "E30.left", {"start": v(38.19, -34.9) * mm, "end": v(38.19, -2.9) * mm});
            skLineSegment(sketch, "E30.right", {"start": v(46.81, -34.9) * mm, "end": v(46.81, -2.9) * mm});
            skSolve(sketch);
        }
        {
            var Q0;
            Q0 = qSketchRegion(id + "F21", true);
            extrude(context, id + "F22", {"entities" : qUnion([Q0]), "operationType" : NewBodyOperationType.ADD, "depth" : 5 * mm, "offsetDistance" : 25 * mm});
        }
        {
            var Q0;
            Q0=makeQuery(id+"F18.opExtrude","CAP_FACE",FACE,{"disambiguationData":[OSD([sQuery(id+"F17.wireOp",EDGE,"E16.1"),sQuery(id+"F17.wireOp",EDGE,"E23"),sQuery(id+"F17.wireOp",EDGE,"E24"),sQuery(id+"F17.wireOp",EDGE,"E25")])],"isStart":true});
            var Q1;
            Q1=makeQuery(id+"F18.opExtrude","CAP_FACE",FACE,{"disambiguationData":[OSD([sQuery(id+"F17.wireOp",EDGE,"E15.0"),sQuery(id+"F17.wireOp",EDGE,"E15.1"),sQuery(id+"F17.wireOp",EDGE,"E15.2"),sQuery(id+"F17.wireOp",EDGE,"E17"),sQuery(id+"F17.wireOp",EDGE,"E18"),sQuery(id+"F17.wireOp",EDGE,"E19")])],"isStart":true});
            extrude(context, id + "F23", {"entities" : qUnion([Q0, Q1]), "operationType" : NewBodyOperationType.REMOVE, "oppositeDirection" : true, "depth" : 5 * mm, "offsetDistance" : 25 * mm});
        }
        {
            var Q0;
            Q0=makeQuery(id+"F18.opExtrude","SWEPT_EDGE",EDGE,{"disambiguationData":[OSD([sQuery(id+"F17.wireOp",EDGE,"E16.1"),sQuery(id+"F17.wireOp",EDGE,"E25")])]});
            var Q1;
            Q1=makeQuery(id+"F18.opExtrude","SWEPT_EDGE",EDGE,{"disambiguationData":[OSD([sQuery(id+"F17.wireOp",EDGE,"E16.1"),sQuery(id+"F17.wireOp",EDGE,"E23")])]});
            fillet(context, id + "F24", {"entities" : qUnion([Q0, Q1]), "radius" : .5 * mm, "tangentPropagation" : true, "allowEdgeOverflow" : false});
        }
        {
            var Q0;
            Q0=makeQuery(id+"F22.opExtrude","CAP_FACE",FACE,{"disambiguationData":[OSD([sQuery(id+"F21.wireOp",EDGE,"E30.bottom"),sQuery(id+"F21.wireOp",EDGE,"E30.top"),sQuery(id+"F21.wireOp",EDGE,"E30.left"),sQuery(id+"F21.wireOp",EDGE,"E30.right")])],"isStart":false});
            var sketch = newSketch(context, id + "F25", { "sketchPlane" : qUnion([Q0])});
            skLineSegment(sketch, "E31.bottom", {"start": v(43.81, -2.9) * mm, "end": v(41.19, -2.9) * mm});
            skLineSegment(sketch, "E31.top", {"start": v(43.81, -34.9) * mm, "end": v(41.19, -34.9) * mm});
            skLineSegment(sketch, "E31.left", {"start": v(43.81, -2.9) * mm, "end": v(43.81, -34.9) * mm});
            skLineSegment(sketch, "E31.right", {"start": v(41.19, -2.9) * mm, "end": v(41.19, -34.9) * mm});
            skPoint(sketch, "E31.middle", {"position": v(42.5, -18.9) * mm});
            skPoint(sketch, "E31.middle.positionSnap0", {"position": v(46.81, -18.9) * mm});
            skPoint(sketch, "E31.middle.positionSnap1", {"position": v(42.5, -2.9) * mm});
            skPoint(sketch, "E31.centerSnap0", {"position": v(46.81, -18.9) * mm});
            skPoint(sketch, "E31.centerSnap1", {"position": v(42.5, -2.9) * mm});
            skSolve(sketch);
        }
        {
            var Q0;
            Q0 = qSketchRegion(id + "F25", true);
            extrude(context, id + "F26", {"entities" : qUnion([Q0]), "operationType" : NewBodyOperationType.REMOVE, "oppositeDirection" : true, "depth" : 2.5 * mm, "offsetDistance" : 25 * mm});
        }
        {
            var Q0;
            Q0=makeQuery(id+"F22.boolean.opBoolean","MERGE",EDGE,{"derivedFrom":[makeQuery(id+"F20.boolean.opBoolean","MERGE",EDGE,{"derivedFrom":[makeQuery(id+"F18.opExtrude","SWEPT_EDGE",EDGE,{"disambiguationData":[OSD([sQuery(id+"F17.wireOp",EDGE,"E17"),sQuery(id+"F17.wireOp",EDGE,"E18")])]}),makeQuery(id+"F20.opExtrude","SWEPT_EDGE",EDGE,{"disambiguationData":[OSD([sQuery(id+"F19.wireOp",EDGE,"E27.0.1"),sQuery(id+"F19.wireOp",EDGE,"E27.0.2")])]})]}),makeQuery(id+"F22.opExtrude","SWEPT_EDGE",EDGE,{"disambiguationData":[OSD([sQuery(id+"F21.wireOp",EDGE,"E30.top"),sQuery(id+"F21.wireOp",EDGE,"E30.left")])]})]});
            var Q1;
            Q1=makeQuery(id+"F22.boolean.opBoolean","MERGE",EDGE,{"derivedFrom":[makeQuery(id+"F20.boolean.opBoolean","MERGE",EDGE,{"derivedFrom":[makeQuery(id+"F18.opExtrude","SWEPT_EDGE",EDGE,{"disambiguationData":[OSD([sQuery(id+"F17.wireOp",EDGE,"E18"),sQuery(id+"F17.wireOp",EDGE,"E19")])]}),makeQuery(id+"F20.opExtrude","SWEPT_EDGE",EDGE,{"disambiguationData":[OSD([sQuery(id+"F19.wireOp",EDGE,"E27.0.0"),sQuery(id+"F19.wireOp",EDGE,"E27.0.1")])]})]}),makeQuery(id+"F22.opExtrude","SWEPT_EDGE",EDGE,{"disambiguationData":[OSD([sQuery(id+"F21.wireOp",EDGE,"E30.top"),sQuery(id+"F21.wireOp",EDGE,"E30.right")])]})]});
            chamfer(context, id + "F27", {"entities" : qUnion([Q0, Q1]), "width" : 2 * mm, "tangentPropagation" : true});
        }
        {
            var Q0;
            Q0=makeQuery(id+"F22.boolean.opBoolean","MERGE",EDGE,{"derivedFrom":[makeQuery(id+"F20.boolean.opBoolean","MERGE",EDGE,{"derivedFrom":[makeQuery(id+"F18.opExtrude","SWEPT_EDGE",EDGE,{"disambiguationData":[OSD([sQuery(id+"F17.wireOp",EDGE,"E24"),sQuery(id+"F17.wireOp",EDGE,"E25")])]}),makeQuery(id+"F20.opExtrude","SWEPT_EDGE",EDGE,{"disambiguationData":[OSD([sQuery(id+"F19.wireOp",EDGE,"E26.bottom"),sQuery(id+"F19.wireOp",EDGE,"E26.right")])]})]}),makeQuery(id+"F22.opExtrude","SWEPT_EDGE",EDGE,{"disambiguationData":[OSD([sQuery(id+"F21.wireOp",EDGE,"E30.bottom"),sQuery(id+"F21.wireOp",EDGE,"E30.right")])]})]});
            var Q1;
            Q1=makeQuery(id+"F22.boolean.opBoolean","MERGE",EDGE,{"derivedFrom":[makeQuery(id+"F20.boolean.opBoolean","MERGE",EDGE,{"derivedFrom":[makeQuery(id+"F18.opExtrude","SWEPT_EDGE",EDGE,{"disambiguationData":[OSD([sQuery(id+"F17.wireOp",EDGE,"E23"),sQuery(id+"F17.wireOp",EDGE,"E24")])]}),makeQuery(id+"F20.opExtrude","SWEPT_EDGE",EDGE,{"disambiguationData":[OSD([sQuery(id+"F19.wireOp",EDGE,"E26.bottom"),sQuery(id+"F19.wireOp",EDGE,"E26.left")])]})]}),makeQuery(id+"F22.opExtrude","SWEPT_EDGE",EDGE,{"disambiguationData":[OSD([sQuery(id+"F21.wireOp",EDGE,"E30.bottom"),sQuery(id+"F21.wireOp",EDGE,"E30.left")])]})]});
            fillet(context, id + "F28", {"entities" : qUnion([Q0, Q1]), "radius" : 1 * mm, "tangentPropagation" : true, "allowEdgeOverflow" : false});
        }
        {
            var Q0;
            {var subQ0=sQuery(id+"F0.wireOp",EDGE,"E0.bottom");Q0=makeQuery(id+"F4.boolean.opBoolean","MERGE",FACE,{"derivedFrom":[makeQuery(id+"F1.opExtrude","CAP_FACE",FACE,{"disambiguationData":[OSD([subQ0,sQuery(id+"F0.wireOp",EDGE,"E0.top"),sQuery(id+"F0.wireOp",EDGE,"E0.left"),sQuery(id+"F0.wireOp",EDGE,"E0.right")])],"isStart":true}),makeQuery(id+"F4.opExtrude","SWEPT_FACE",FACE,{"disambiguationData":[OSD([subQ0]),TDD([makeQuery(id+"F1.opExtrude","CAP_EDGE",EDGE,{"disambiguationData":[OSD([subQ0])],"isStart":true})])]})]});}
            var sketch = newSketch(context, id + "F29", { "sketchPlane" : qUnion([Q0])});
            skLineSegment(sketch, "E32.bottom", {"start": v(75, -37.5) * mm, "end": v(85, -37.5) * mm});
            skLineSegment(sketch, "E32.top", {"start": v(75, -47.5) * mm, "end": v(85, -47.5) * mm});
            skLineSegment(sketch, "E32.left", {"start": v(75, -37.5) * mm, "end": v(75, -47.5) * mm});
            skLineSegment(sketch, "E32.right", {"start": v(85, -37.5) * mm, "end": v(85, -47.5) * mm});
            skPoint(sketch, "E32.middle", {"position": v(80, -42.5) * mm});
            skPoint(sketch, "E32.middle.positionSnap0", {"position": v(80, -37.5) * mm});
            skPoint(sketch, "E32.centerSnap0", {"position": v(80, -37.5) * mm});
            skCircle(sketch, "E33", {"center": v(80, -42.5) * mm, "radius": 1 * mm});
            skSolve(sketch);
        }
        {
            var Q0;
            Q0 = qSketchRegion(id + "F29", true);
            extrude(context, id + "F30", {"entities" : qUnion([Q0]), "operationType" : NewBodyOperationType.ADD, "oppositeDirection" : true, "depth" : 3 * mm, "offsetDistance" : 25 * mm});
        }
        {
            var Q0;
            Q0=makeQuery(id+"F30.opExtrude","SWEPT_EDGE",EDGE,{"disambiguationData":[OSD([sQuery(id+"F29.wireOp",EDGE,"E32.top"),sQuery(id+"F29.wireOp",EDGE,"E32.left")])]});
            var Q1;
            Q1=makeQuery(id+"F30.opExtrude","SWEPT_EDGE",EDGE,{"disambiguationData":[OSD([sQuery(id+"F29.wireOp",EDGE,"E32.top"),sQuery(id+"F29.wireOp",EDGE,"E32.right")])]});
            var Q2;
            Q2=makeQuery(id+"F30.opExtrude","SWEPT_EDGE",EDGE,{"disambiguationData":[OSD([sQuery(id+"F0.wireOp",EDGE,"E0.top"),sQuery(id+"F29.wireOp",EDGE,"E32.bottom"),sQuery(id+"F29.wireOp",EDGE,"E32.right")])]});
            var Q3;
            Q3=makeQuery(id+"F30.opExtrude","SWEPT_EDGE",EDGE,{"disambiguationData":[OSD([sQuery(id+"F0.wireOp",EDGE,"E0.top"),sQuery(id+"F29.wireOp",EDGE,"E32.bottom"),sQuery(id+"F29.wireOp",EDGE,"E32.left")])]});
            chamfer(context, id + "F31", {"entities" : qUnion([Q0, Q1, Q2, Q3]), "width" : 2.5 * mm, "tangentPropagation" : true});
        }
        {
            var Q0;
            Q0=makeQuery(id+"F18.opExtrude","CAP_FACE",FACE,{"disambiguationData":[OSD([sQuery(id+"F17.wireOp",EDGE,"E16.1"),sQuery(id+"F17.wireOp",EDGE,"E23"),sQuery(id+"F17.wireOp",EDGE,"E24"),sQuery(id+"F17.wireOp",EDGE,"E25")])],"isStart":false});
            extrude(context, id + "F32", {"entities" : qUnion([Q0]), "operationType" : NewBodyOperationType.REMOVE, "oppositeDirection" : true, "depth" : 1 * mm, "offsetDistance" : 25 * mm});
        }
    });
